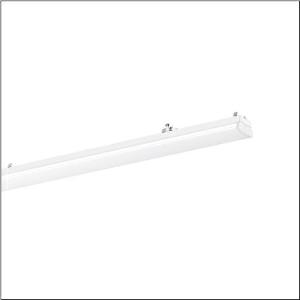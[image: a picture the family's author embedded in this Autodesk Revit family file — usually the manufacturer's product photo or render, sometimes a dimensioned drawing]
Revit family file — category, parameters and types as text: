
# Revit family: licross_r__21_recessed_opal_mo_52tl1dcn485g_66e6
name_source: partatom
category: Lighting Fixtures
units: mm (PartAtom-declared; Revit-internal decimal feet)

## family parameters
Cut with Voids When Loaded = No
Host = Face
Light Source = No
Part Type = Normal
Room Calculation Point = No
Round Connector Dimension = Use Diameter
Shared = No

## types (1)
- --- (1 x LED, 8780 lm, 49.9 W, 4000K)
    Apparent Load = 50 VA
    CIE Flux Codes = 44 73 91 87 100
    Color Rendering = 80
    Color Temperature = 4000K
    Default Elevation = 1800 mm
    Description = Licross® 21 recessed opal MO, luminaire insert, of sheet steel, galvanised, coil coated, white, length: 1.500mm, width: 66mm, height: 67mm, LED rated luminous flux: 8.780lm, light colour: 840, control gear: ON/OFF Multilumen, CLOi, with plug, 3-pole, with phase selection, mains connection: 220..240V, AC, 50/60Hz, start of lifetime: 50W, end of service life: 61W, halogen-free wiring, primary optical cover: cover, of PMMA, light emission: direct with ceiling illumination distribution, primary light characteristic: symmetric, protection rating (complete): IP40, insulation class (complete): insulation class I (protective earthing), certification: CE, ENEC, VDE, UKCA, protection symbol: D if used in an environment without relevant dust loads with corresponding accessories, impact resistance: IK06, permissible ambient temperature for indoor applications: -35..+40°C, corresponds to IFS (International Featured Standards) requirements for safety and quality in the food industry, reducing of maximum allowable ambient temperature of 5°C with ceiling mounting, LABS conformity tested according to VDMA 24364:2018-05, packaging unit: 1 piece
    Height = 83 mm
    Lamp = 1 x LED
    Lamp Light Flux = 8780 lm
    Lamp Power = 49.9 W
    Lamp count = 1
    Length = 1500 mm
    Luminous efficacy = 176 lm/W
    Manufacturer = Siteco
    ModVariant = No
    Model = 52TL1DCN485G
    Mounting Place = Ceiling
    Mounting Type = Pendant
    Number of Poles = 1
    OnlyDefault = Yes
    Power Factor = 1
    Product Name = Licross® 21 recessed opal MO
    Product group = luminaire insert
    ProductGroupID = 901
    Protection Class = Protection class I
    Protection Degree = IP 40
    RLX_Detail_Level = 1
    RLX_Emergency_Light_Flux = 0 lm
    RLX_Emergency_Type = 0
    RLX_Emergency_Type_DB = No
    RlxData = <blob elided: 24753 chars, md5=82550266>
    Socket = socket
    Standby Power = 0 W
    System Light Flux = 8780 lm
    System Power = 50 W
    Type Comments = factory setting: luminous flux: 100 % | (A | C | E) | 116 mA
    Type Image = l_1313666.jpg
    URL = http://relux.com
    VarID = @adj_027045
    Voltage = 0 V
    Weight = 0.00 kg
    Width = 76 mm

## geometry (parser evidence)
native form markers: Blend x4, Sweep x11
no freeform markers — native parametric forms only
